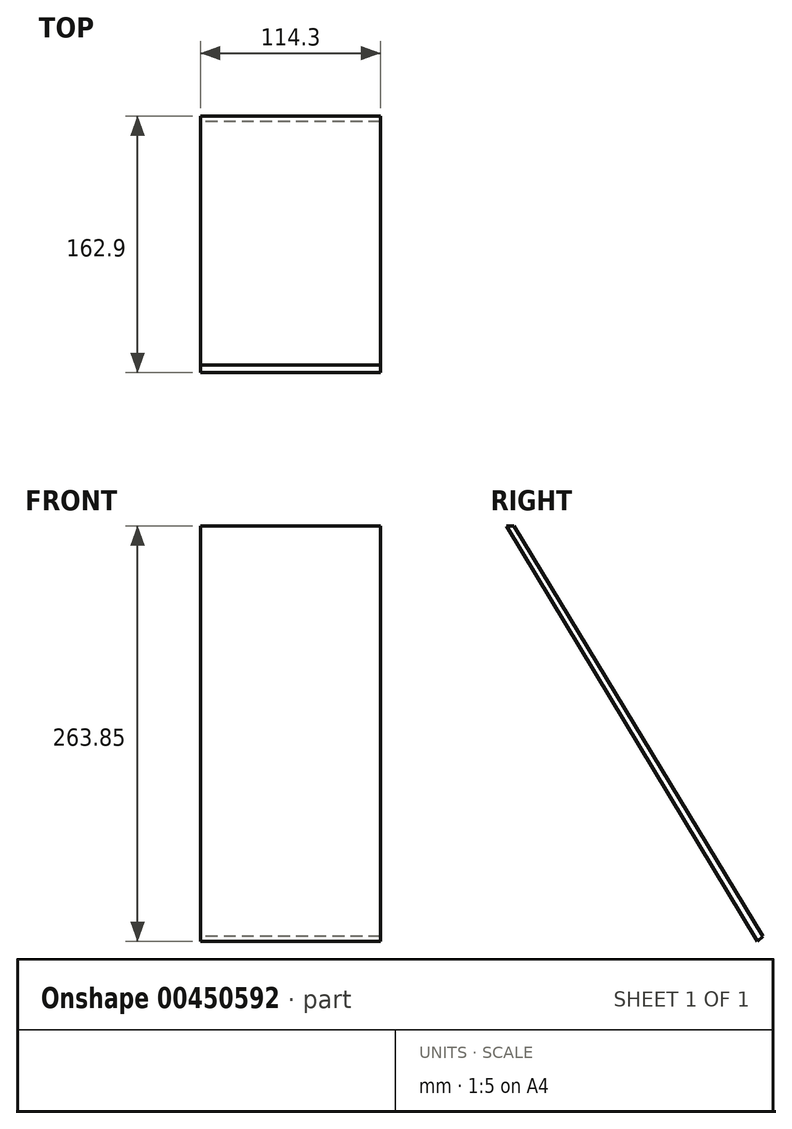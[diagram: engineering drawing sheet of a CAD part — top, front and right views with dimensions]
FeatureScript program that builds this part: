
annotation { "Feature Type Name" : "Feature", "Feature Type Description" : "" }
export const myFeature = defineFeature(function(context is Context, id is Id, definition is map)
    precondition{}
    {
        {
            var Q0;
            Q0=qCreatedBy(makeId("Right.planeOp"),FACE);
            var sketch = newSketch(context, id + "F0", { "sketchPlane" : qUnion([Q0])});
            skLineSegment(sketch, "E0.left", {"start": v(-57.23, 36.82) * mm, "end": v(102.2, -227.03) * mm});
            skLineSegment(sketch, "E0.right", {"start": v(-52.46, 36.8) * mm, "end": v(105.67, -223.77) * mm});
            skPoint(sketch, "E0.middle", {"position": v(0, 0) * mm});
            skLineSegment(sketch, "E1", {"start": v(-57.23, 36.82) * mm, "end": v(-52.46, 36.8) * mm});
            skLineSegment(sketch, "E2", {"start": v(102.2, -227.03) * mm, "end": v(105.67, -223.77) * mm});
            skSolve(sketch);
        }
        {
            var Q0;
            Q0=makeQuery(id+"F0.imprint","IMPRINT",FACE,{"disambiguationData":[TD([[makeQuery(id+"F0.imprint","IMPRINT",EDGE,{"derivedFrom":sQuery(id+"F0.wireOp",EDGE,"E0.left")}),1.0]])]});
            extrude(context, id + "F1", {"entities" : qUnion([Q0]), "depth" : 114.3 * mm});
        }
    });
